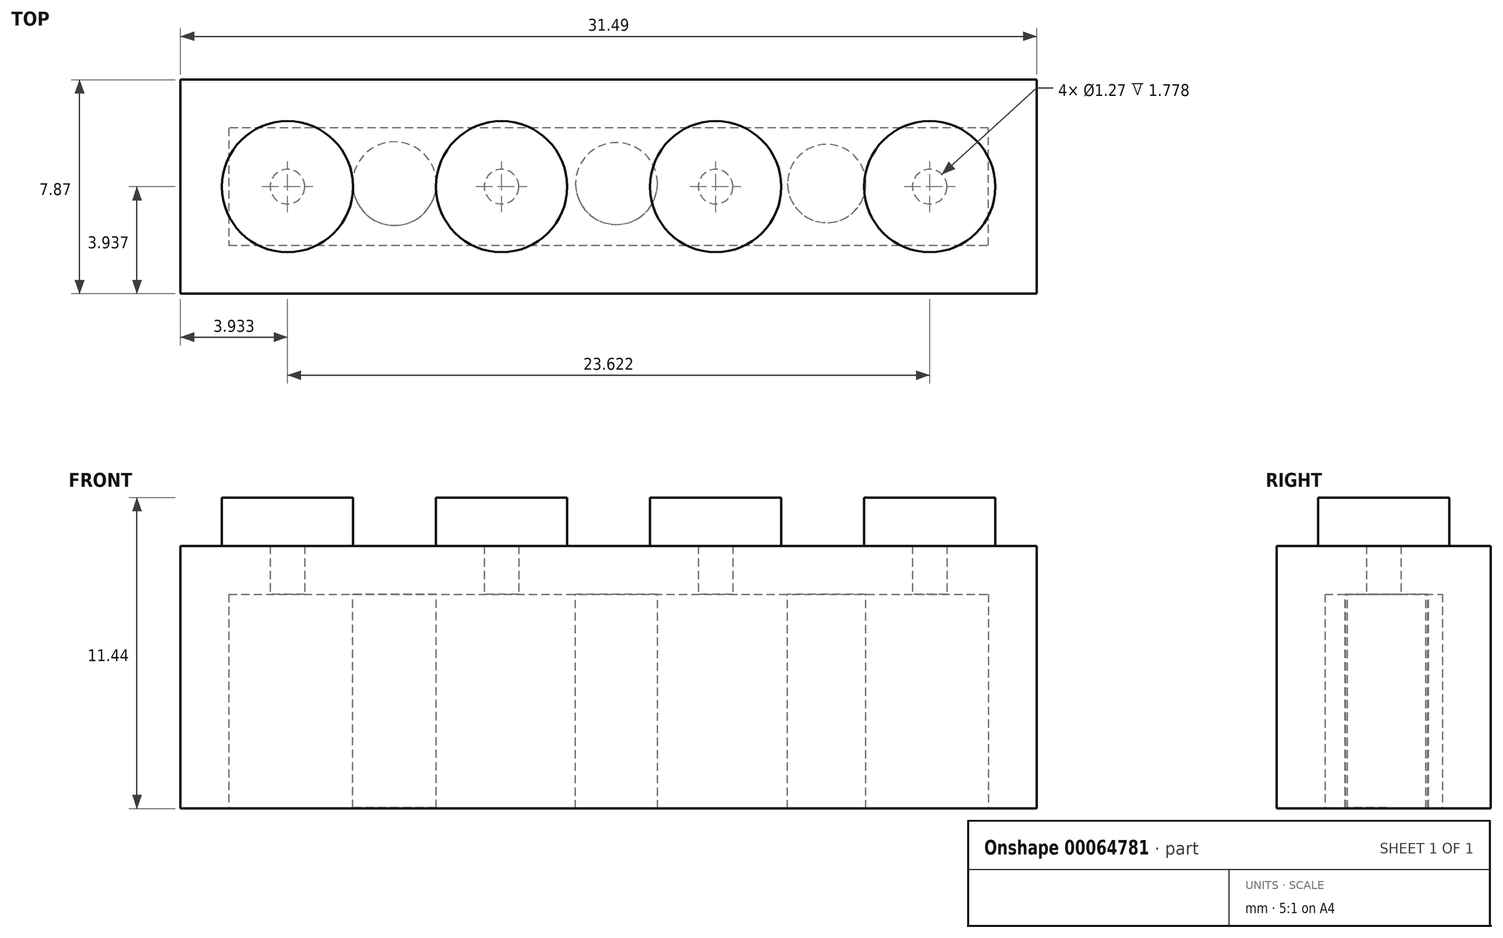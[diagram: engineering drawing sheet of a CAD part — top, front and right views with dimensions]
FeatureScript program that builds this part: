
annotation { "Feature Type Name" : "Feature", "Feature Type Description" : "" }
export const myFeature = defineFeature(function(context is Context, id is Id, definition is map)
    precondition{}
    {
        {
            var Q0;
            Q0=qCreatedBy(makeId("Top.planeOp"),FACE);
            var sketch = newSketch(context, id + "F0", { "sketchPlane" : qUnion([Q0])});
            skLineSegment(sketch, "E0", {"start": v(0, 0) * mm, "end": v(23.62, 0) * mm});
            skLineSegment(sketch, "E1", {"start": v(23.62, 0) * mm, "end": v(23.62, 7.87) * mm});
            skLineSegment(sketch, "E2", {"start": v(23.62, 7.87) * mm, "end": v(-7.87, 7.87) * mm});
            skLineSegment(sketch, "E3", {"start": v(-7.87, 7.87) * mm, "end": v(-7.87, 0) * mm});
            skLineSegment(sketch, "E4", {"start": v(-7.87, 0) * mm, "end": v(23.62, 0) * mm});
            skPoint(sketch, "E5.centerSnap0", {"position": v(23.62, 3.94) * mm});
            skPoint(sketch, "E6.centerSnap0", {"position": v(11.81, 0) * mm});
            skSolve(sketch);
        }
        {
            var Q0;
            Q0 = qSketchRegion(id + "F0", true);
            extrude(context, id + "F1", {"entities" : qUnion([Q0]), "depth" : 9.65 * mm});
        }
        {
            var Q0;
            Q0=makeQuery(id+"F1.opExtrude","CAP_FACE",FACE,{"disambiguationData":[OSD([sQuery(id+"F0.wireOp",EDGE,"E1"),sQuery(id+"F0.wireOp",EDGE,"E2"),sQuery(id+"F0.wireOp",EDGE,"E3"),sQuery(id+"F0.wireOp",EDGE,"E4")])],"isStart":false});
            var sketch = newSketch(context, id + "F2", { "sketchPlane" : qUnion([Q0])});
            skCircle(sketch, "E7", {"center": v(19.69, 3.94) * mm, "radius": 2.41 * mm});
            skPoint(sketch, "E7.centerSnap0", {"position": v(23.62, 3.94) * mm});
            skLineSegment(sketch, "E8", {"start": v(22.1, 3.94) * mm, "end": v(23.62, 3.94) * mm});
            skCircle(sketch, "E9", {"center": v(11.81, 3.94) * mm, "radius": 2.41 * mm});
            skCircle(sketch, "E10", {"center": v(3.94, 3.94) * mm, "radius": 2.41 * mm});
            skCircle(sketch, "E11", {"center": v(-3.94, 3.94) * mm, "radius": 2.41 * mm});
            skSolve(sketch);
        }
        {
            var Q0;
            Q0=makeQuery(id+"F2.imprint","IMPRINT",FACE,{"disambiguationData":[TD([[makeQuery(id+"F2.imprint","IMPRINT",EDGE,{"derivedFrom":sQuery(id+"F2.wireOp",EDGE,"E7")}),1.0]])]});
            extrude(context, id + "F3", {"entities" : qUnion([Q0]), "operationType" : NewBodyOperationType.ADD, "depth" : 1.78 * mm});
        }
        {
            var Q0;
            Q0=makeQuery(id+"F2.imprint","IMPRINT",FACE,{"disambiguationData":[TD([[makeQuery(id+"F2.imprint","IMPRINT",EDGE,{"derivedFrom":sQuery(id+"F2.wireOp",EDGE,"E9")}),1.0]])]});
            extrude(context, id + "F4", {"entities" : qUnion([Q0]), "operationType" : NewBodyOperationType.ADD, "depth" : 1.78 * mm});
        }
        {
            var Q0;
            Q0=makeQuery(id+"F2.imprint","IMPRINT",FACE,{"disambiguationData":[TD([[makeQuery(id+"F2.imprint","IMPRINT",EDGE,{"derivedFrom":sQuery(id+"F2.wireOp",EDGE,"E10")}),1.0]])]});
            extrude(context, id + "F5", {"entities" : qUnion([Q0]), "operationType" : NewBodyOperationType.ADD, "depth" : 1.78 * mm});
        }
        {
            var Q0;
            Q0=makeQuery(id+"F2.imprint","IMPRINT",FACE,{"disambiguationData":[TD([[makeQuery(id+"F2.imprint","IMPRINT",EDGE,{"derivedFrom":sQuery(id+"F2.wireOp",EDGE,"E11")}),1.0]])]});
            extrude(context, id + "F6", {"entities" : qUnion([Q0]), "operationType" : NewBodyOperationType.ADD, "depth" : 1.78 * mm});
        }
        {
            var Q0;
            Q0=makeQuery(id+"F1.opExtrude","CAP_FACE",FACE,{"disambiguationData":[OSD([sQuery(id+"F0.wireOp",EDGE,"E1"),sQuery(id+"F0.wireOp",EDGE,"E2"),sQuery(id+"F0.wireOp",EDGE,"E3"),sQuery(id+"F0.wireOp",EDGE,"E4")])],"isStart":true});
            shell(context, id + "F7", {"entities" : qUnion([Q0]), "thickness" : 1.78 * mm});
        }
        {
            var Q0;
            Q0=makeQuery(id+"F7.opShell","OFFSET_FACE",FACE,{"disambiguationData":[OSD([sQuery(id+"F0.wireOp",EDGE,"E1"),sQuery(id+"F0.wireOp",EDGE,"E2"),sQuery(id+"F0.wireOp",EDGE,"E3"),sQuery(id+"F0.wireOp",EDGE,"E4")])]});
            var sketch = newSketch(context, id + "F8", { "sketchPlane" : qUnion([Q0])});
            skCircle(sketch, "E12", {"center": v(15.9, -4.05) * mm, "radius": 1.44 * mm});
            skCircle(sketch, "E13", {"center": v(8.16, -4.05) * mm, "radius": 1.5 * mm});
            skCircle(sketch, "E14", {"center": v(0, -4.05) * mm, "radius": 1.54 * mm});
            skSolve(sketch);
        }
        {
            var Q0;
            Q0=makeQuery(id+"F8.imprint","IMPRINT",FACE,{"disambiguationData":[TD([[makeQuery(id+"F8.imprint","IMPRINT",EDGE,{"derivedFrom":sQuery(id+"F8.wireOp",EDGE,"E12")}),1.0]])]});
            extrude(context, id + "F9", {"entities" : qUnion([Q0]), "operationType" : NewBodyOperationType.ADD, "depth" : 7.87 * mm});
        }
        {
            var Q0;
            Q0=makeQuery(id+"F8.imprint","IMPRINT",FACE,{"disambiguationData":[TD([[makeQuery(id+"F8.imprint","IMPRINT",EDGE,{"derivedFrom":sQuery(id+"F8.wireOp",EDGE,"E13")}),1.0]])]});
            extrude(context, id + "F10", {"entities" : qUnion([Q0]), "operationType" : NewBodyOperationType.ADD, "depth" : 7.88 * mm});
        }
        {
            var Q0;
            Q0=makeQuery(id+"F8.imprint","IMPRINT",FACE,{"disambiguationData":[TD([[makeQuery(id+"F8.imprint","IMPRINT",EDGE,{"derivedFrom":sQuery(id+"F8.wireOp",EDGE,"E14")}),1.0]])]});
            extrude(context, id + "F11", {"entities" : qUnion([Q0]), "operationType" : NewBodyOperationType.ADD, "depth" : 7.85 * mm});
        }
    });
